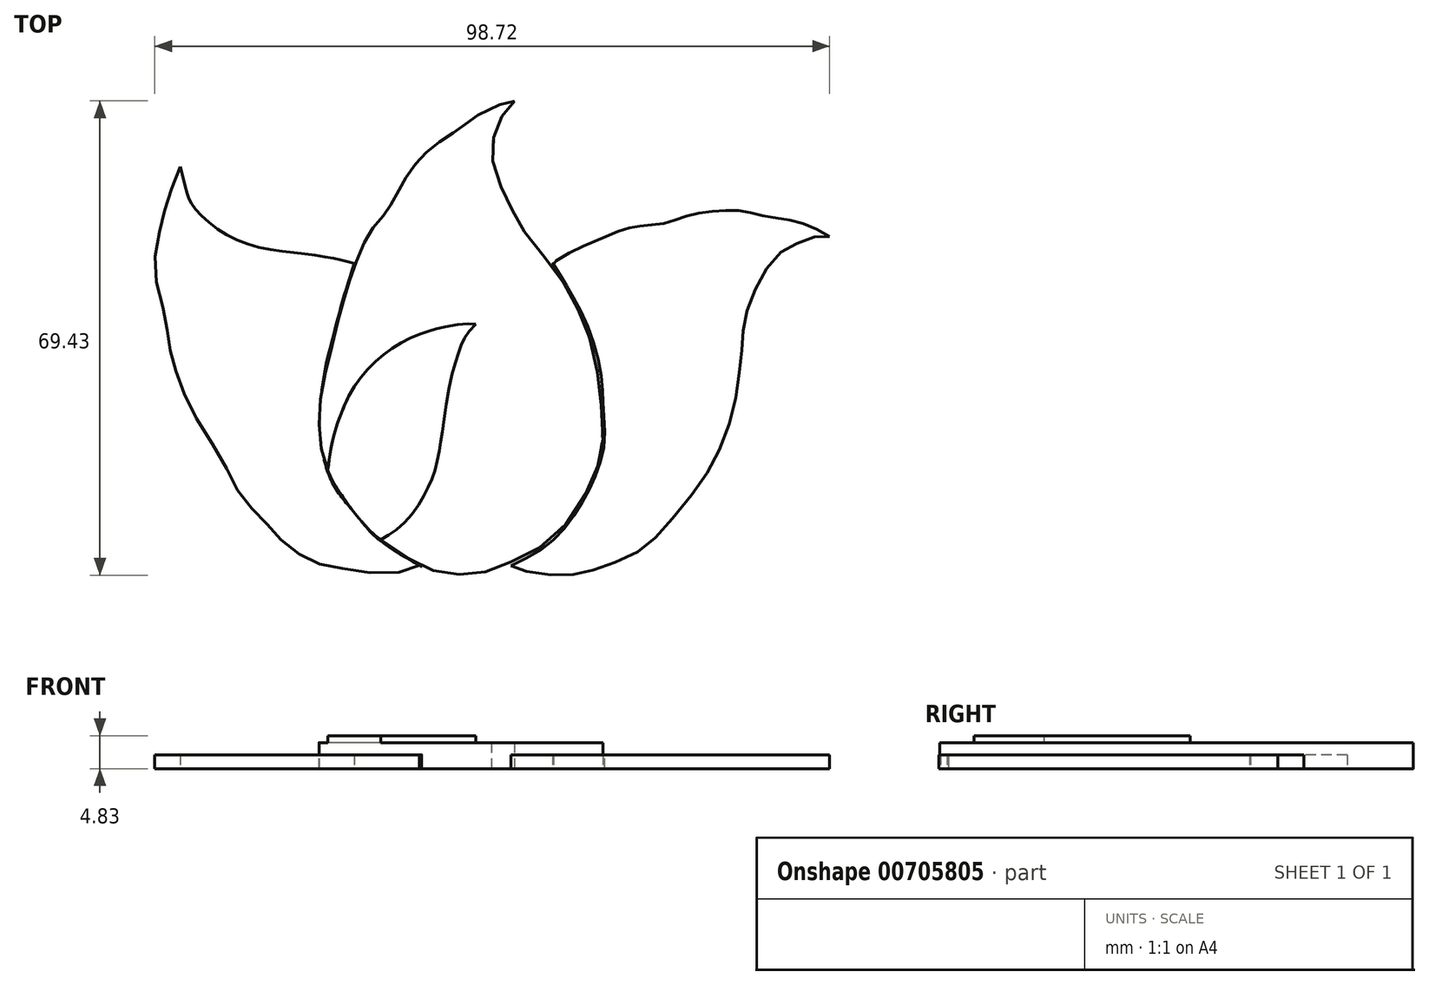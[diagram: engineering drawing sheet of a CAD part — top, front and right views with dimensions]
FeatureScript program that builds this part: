
annotation { "Feature Type Name" : "Feature", "Feature Type Description" : "" }
export const myFeature = defineFeature(function(context is Context, id is Id, definition is map)
    precondition{}
    {
        {
            var Q0;
            Q0=qCreatedBy(makeId("Top.planeOp"),FACE);
            var sketch = newSketch(context, id + "F0", { "sketchPlane" : qUnion([Q0])});
            skFitSpline(sketch, "E0", {"points": [v(-39.16, 34.9) * mm, v(-41, 30) * mm, v(-42.2, 25.32) * mm, v(-42.86, 19.44) * mm, v(-41.44, 13.34) * mm, v(-40.8, 8.77) * mm, v(-39.7, 4.75) * mm, v(-37.3, -1.02) * mm, v(-32.95, -8.2) * mm, v(-30.23, -13.32) * mm, v(-26.97, -16.91) * mm, v(-24.14, -19.96) * mm, v(-19.78, -22.9) * mm, v(-14.89, -23.99) * mm, v(-7.05, -24.42) * mm, v(-3.9, -23.44) * mm, v(-3.9, -23.77) * mm], "startDerivative": vector(-31.07, -76.49) * mm, "endDerivative": vector(-6.78, -25.99) * mm});
            skFitSpline(sketch, "E1", {"points": [v(-39.16, 34.9) * mm, v(-38.07, 30.76) * mm, v(-37.42, 29.34) * mm, v(-34.26, 26.19) * mm, v(-28.17, 23.25) * mm, v(-20.98, 22.16) * mm, v(-16.3, 21.4) * mm, v(-13.69, 20.75) * mm], "startDerivative": vector(8.42, -33.55) * mm, "endDerivative": vector(21.74, -5.87) * mm});
            skFitSpline(sketch, "E2", {"points": [v(-13.69, 20.75) * mm, v(-15.43, 15.2) * mm, v(-16.74, 10.3) * mm, v(-17.83, 5.94) * mm, v(-18.48, 2.13) * mm, v(-18.7, -4.07) * mm, v(-16.95, -11.25) * mm, v(-13.69, -15.72) * mm, v(-10.53, -19.3) * mm, v(-3.86, -23.63) * mm], "startDerivative": vector(-16.19, -49.7) * mm, "endDerivative": vector(56.48, -32.09) * mm});
            skSolve(sketch);
        }
        {
            var Q0;
            Q0 = qSketchRegion(id + "F0", true);
            extrude(context, id + "F1", {"entities" : qUnion([Q0]), "depth" : 2.03 * mm, "offsetDistance" : 25.4 * mm});
        }
        {
            var Q0;
            Q0=qCreatedBy(makeId("Top.planeOp"),FACE);
            var sketch = newSketch(context, id + "F2", { "sketchPlane" : qUnion([Q0])});
            skFitSpline(sketch, "E3", {"points": [v(9.74, 44.52) * mm, v(4.81, 42.7) * mm, v(1.92, 40.66) * mm, v(-0.98, 38.73) * mm, v(-3.87, 36.27) * mm, v(-6.12, 33.37) * mm, v(-7.62, 30.7) * mm, v(-9.23, 28.01) * mm, v(-11.26, 25.55) * mm, v(-13.51, 20.73) * mm, v(-15.33, 15.05) * mm, v(-17.26, 7.55) * mm, v(-18.87, -1.99) * mm, v(-17.7, -9.28) * mm, v(-15.44, -13.35) * mm, v(-11.37, -18.38) * mm, v(-6.98, -21.7) * mm, v(-3.12, -23.85) * mm, v(0, -24.6) * mm, v(3.63, -24.7) * mm, v(7.17, -23.85) * mm, v(10.92, -22.13) * mm, v(15.42, -19.35) * mm, v(19.7, -13.78) * mm, v(21.63, -9.6) * mm, v(22.6, -6.06) * mm, v(22.5, -1.13) * mm, v(21.85, 5.08) * mm, v(20.35, 10.98) * mm, v(18.53, 15.05) * mm, v(16.17, 19.12) * mm, v(12.95, 23.09) * mm, v(10.28, 26.84) * mm, v(9, 29.4) * mm, v(7.6, 32.3) * mm, v(6.53, 35.84) * mm, v(6.53, 38.62) * mm, v(7.5, 41.4) * mm, v(8.45, 43.02) * mm, v(9.74, 44.52) * mm]});
            skSolve(sketch);
        }
        {
            var Q0;
            Q0 = qSketchRegion(id + "F2", true);
            extrude(context, id + "F3", {"entities" : qUnion([Q0]), "depth" : 3.8 * mm, "offsetDistance" : 25.4 * mm});
        }
        {
            var Q0;
            Q0=qCreatedBy(makeId("Top.planeOp"),FACE);
            var sketch = newSketch(context, id + "F4", { "sketchPlane" : qUnion([Q0])});
            skFitSpline(sketch, "E4", {"points": [v(55.82, 24.7) * mm, v(51.27, 26.84) * mm, v(46.9, 27.58) * mm, v(43.2, 28.42) * mm, v(39.38, 28.42) * mm, v(35.2, 27.77) * mm, v(32.14, 26.75) * mm, v(28.7, 26.28) * mm, v(25.92, 25.82) * mm, v(22.4, 24.33) * mm, v(18.87, 22.85) * mm, v(15.34, 20.71) * mm, v(15.43, 20.62) * mm], "startDerivative": vector(-43.98, 24.84) * mm, "endDerivative": vector(9.34, -3.96) * mm});
            skFitSpline(sketch, "E5", {"points": [v(55.82, 24.7) * mm, v(53.96, 24.7) * mm, v(51.27, 23.78) * mm, v(48.85, 22.48) * mm, v(46.25, 19.41) * mm, v(44.21, 15.14) * mm, v(43.28, 11.52) * mm, v(43, 8.37) * mm, v(42.54, 4) * mm, v(41.52, -1.57) * mm, v(39.2, -7.6) * mm, v(36.23, -12.43) * mm, v(31.59, -18) * mm, v(28.43, -21.06) * mm, v(23.7, -23.29) * mm, v(19.8, -24.5) * mm, v(16.36, -24.87) * mm, v(11.35, -24.3) * mm, v(9.21, -23.47) * mm], "startDerivative": vector(-47.7, 4.68) * mm, "endDerivative": vector(-44.21, 21.86) * mm});
            skFitSpline(sketch, "E6", {"points": [v(9.21, -23.47) * mm, v(13.58, -21.15) * mm, v(16.73, -18.37) * mm, v(19.33, -14.75) * mm, v(21, -11.6) * mm, v(22.4, -7.88) * mm, v(22.95, -4.07) * mm, v(22.67, 0) * mm, v(22.58, 2.52) * mm, v(21.93, 6.88) * mm, v(20.35, 11.8) * mm, v(18.4, 15.7) * mm, v(16.83, 18.4) * mm, v(15.43, 20.62) * mm], "startDerivative": vector(53.03, 25.3) * mm, "endDerivative": vector(-21.97, 34.77) * mm});
            skSolve(sketch);
        }
        {
            var Q0;
            Q0 = qSketchRegion(id + "F4", true);
            extrude(context, id + "F5", {"entities" : qUnion([Q0]), "depth" : 2.03 * mm, "offsetDistance" : 25.4 * mm});
        }
        {
            var Q0;
            Q0=makeQuery(id+"F3.opExtrude","CAP_FACE",FACE,{"disambiguationData":[OSD([sQuery(id+"F2.wireOp",EDGE,"E3")])],"isStart":false});
            var sketch = newSketch(context, id + "F6", { "sketchPlane" : qUnion([Q0])});
            skFitSpline(sketch, "E7", {"points": [v(-9.85, -19.7) * mm, v(-7.37, -18.1) * mm, v(-4.65, -15.18) * mm, v(-2.95, -12.1) * mm, v(-1.92, -9.67) * mm, v(-1.26, -6.52) * mm, v(-0.71, -3.25) * mm, v(0.44, 3.9) * mm, v(1.65, 7.9) * mm, v(2.38, 9.77) * mm, v(4.07, 11.9) * mm], "startDerivative": vector(26.6, 15.2) * mm, "endDerivative": vector(22.02, 24.24) * mm});
            skFitSpline(sketch, "E8", {"points": [v(4.07, 11.9) * mm, v(2.2, 11.9) * mm, v(-1.26, 11.28) * mm, v(-2.7, 10.86) * mm, v(-5.13, 10.01) * mm, v(-7.62, 8.68) * mm, v(-9.98, 6.98) * mm, v(-12.16, 4.74) * mm, v(-14.04, 2.2) * mm, v(-15.43, -0.7) * mm, v(-16.16, -2.65) * mm, v(-16.58, -4.1) * mm, v(-17.19, -6.58) * mm, v(-17.6, -9.5) * mm, v(-17.62, -9.45) * mm], "startDerivative": vector(-25.36, 1.6) * mm, "endDerivative": vector(-1.6, 7.85) * mm});
            skFitSpline(sketch, "E9", {"points": [v(-17.6, -9.5) * mm, v(-16.83, -11.15) * mm, v(-15.6, -13.1) * mm, v(-14.09, -15.23) * mm, v(-12.78, -16.87) * mm, v(-11.3, -18.44) * mm, v(-9.85, -19.7) * mm], "startDerivative": vector(4.68, -10.54) * mm, "endDerivative": vector(9.06, -7.8) * mm});
            skSolve(sketch);
        }
        {
            var Q0;
            Q0 = qSketchRegion(id + "F6", true);
            extrude(context, id + "F7", {"entities" : qUnion([Q0]), "operationType" : NewBodyOperationType.ADD, "depth" : 1.02 * mm, "offsetDistance" : 25.4 * mm});
        }
        {
            var Q0;
            Q0=qCreatedBy(makeId("Top.planeOp"),FACE);
            var sketch = newSketch(context, id + "F8", { "sketchPlane" : qUnion([Q0])});
            skCircle(sketch, "E10", {"center": v(-26.6, -53.42) * mm, "radius": 16.64 * mm});
            skSolve(sketch);
        }
        {
            var Q0;
            Q0=sQuery(id+"F8.wireOp",EDGE,"E10");
            extrude(context, id + "F9", {"bodyType" : ToolBodyType.SURFACE, "surfaceEntities" : qUnion([Q0]), "depth" : 25.4 * mm, "offsetDistance" : 25.4 * mm});
        }
    });
